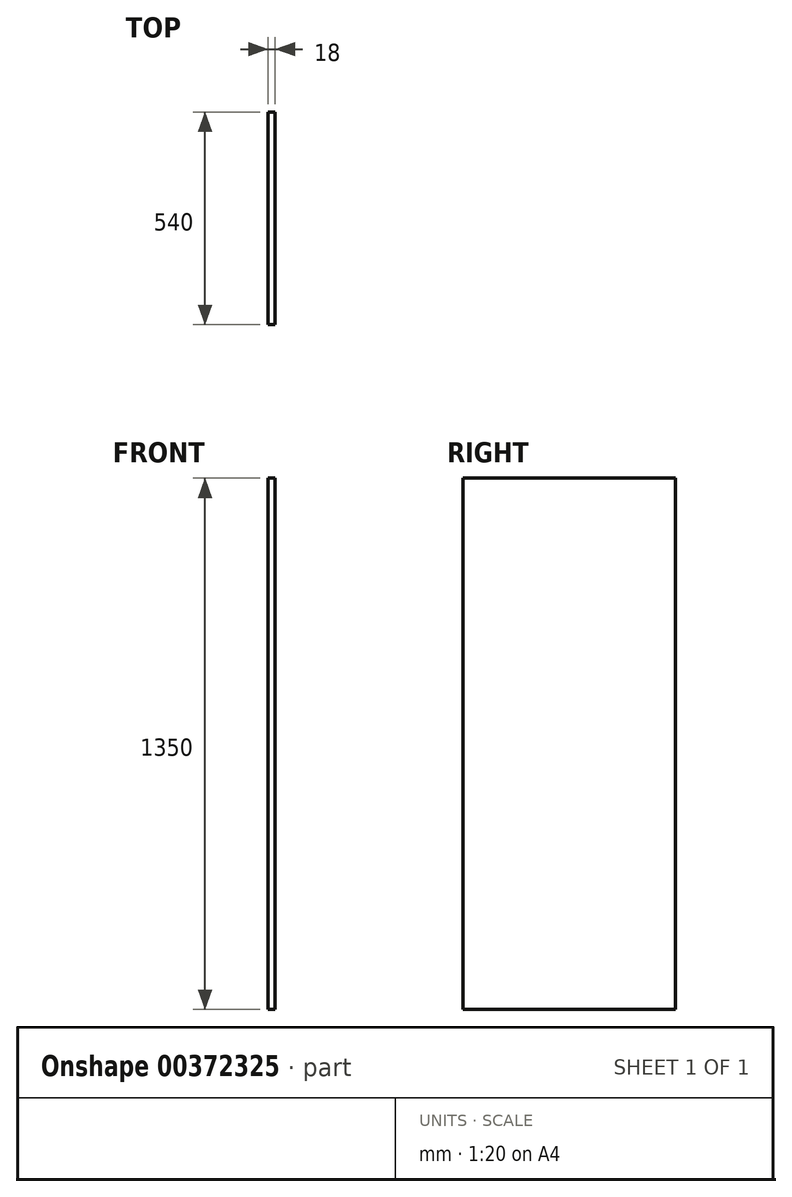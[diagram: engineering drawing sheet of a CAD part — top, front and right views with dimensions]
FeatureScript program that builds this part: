
annotation { "Feature Type Name" : "Feature", "Feature Type Description" : "" }
export const myFeature = defineFeature(function(context is Context, id is Id, definition is map)
    precondition{}
    {
        {
            var Q0;
            Q0=qCreatedBy(makeId("Right.planeOp"),FACE);
            var sketch = newSketch(context, id + "F0", { "sketchPlane" : qUnion([Q0])});
            skLineSegment(sketch, "E0.bottom", {"start": v(0, 0) * mm, "end": v(540, 0) * mm});
            skLineSegment(sketch, "E0.top", {"start": v(0, 1350) * mm, "end": v(540, 1350) * mm});
            skLineSegment(sketch, "E0.left", {"start": v(0, 0) * mm, "end": v(0, 1350) * mm});
            skLineSegment(sketch, "E0.right", {"start": v(540, 0) * mm, "end": v(540, 1350) * mm});
            skSolve(sketch);
        }
        {
            var Q0;
            Q0=makeQuery(id+"F0.imprint","IMPRINT",FACE,{"disambiguationData":[TD([[makeQuery(id+"F0.imprint","IMPRINT",EDGE,{"derivedFrom":sQuery(id+"F0.wireOp",EDGE,"E0.bottom")}),1.0]])]});
            extrude(context, id + "F1", {"entities" : qUnion([Q0]), "depth" : 18 * mm});
        }
    });
